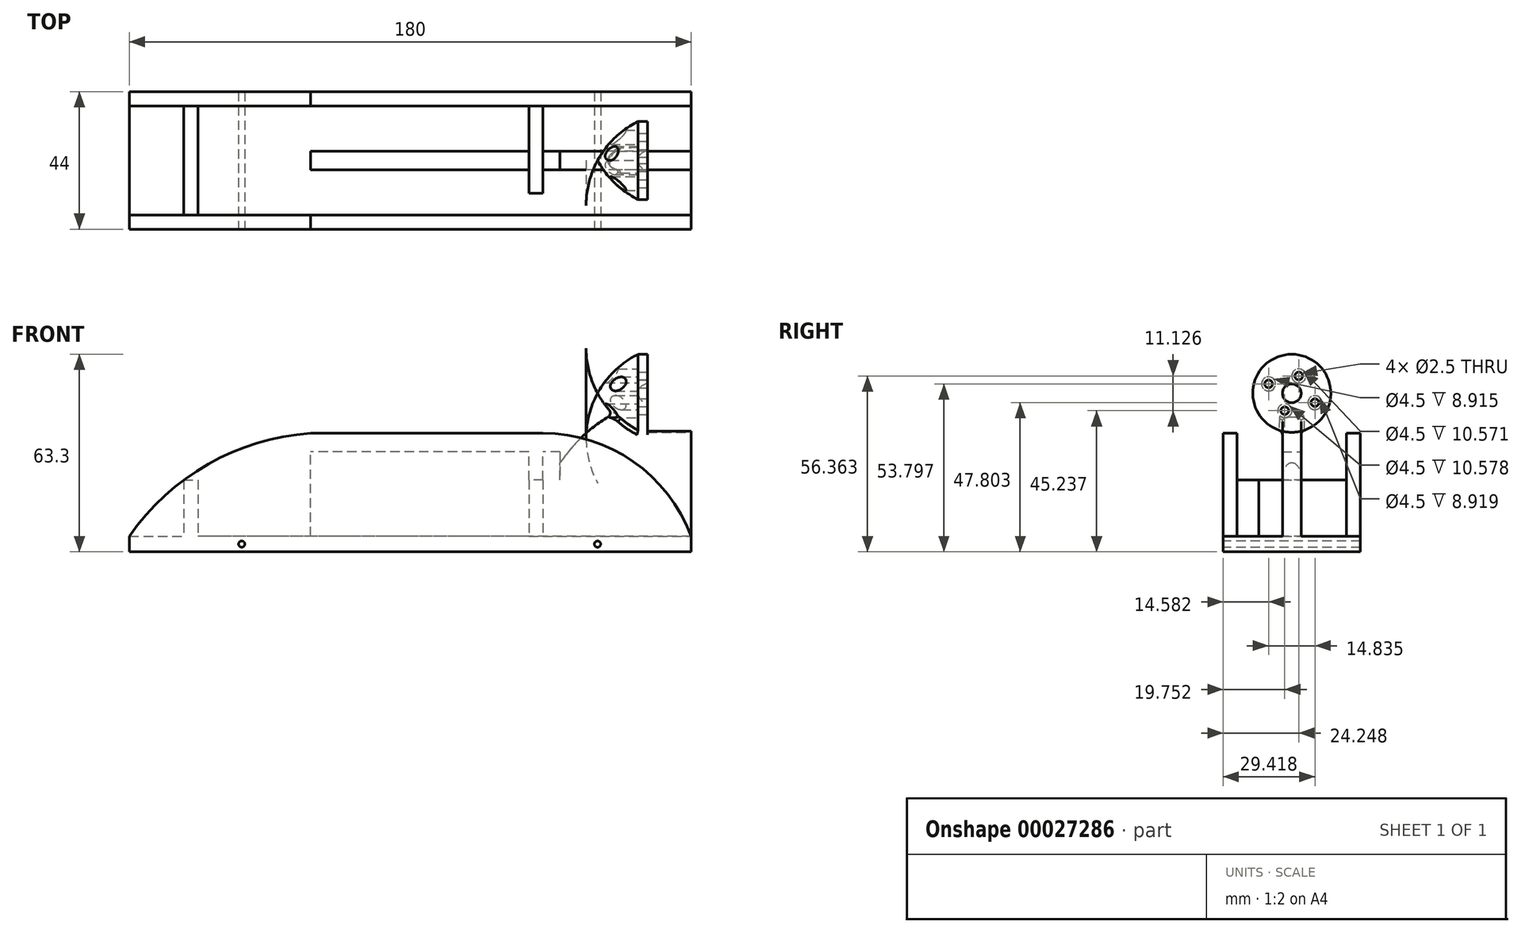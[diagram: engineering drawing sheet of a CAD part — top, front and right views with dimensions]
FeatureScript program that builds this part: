
annotation { "Feature Type Name" : "Feature", "Feature Type Description" : "" }
export const myFeature = defineFeature(function(context is Context, id is Id, definition is map)
    precondition{}
    {
        {
            var Q0;
            Q0=qCreatedBy(makeId("Top.planeOp"),FACE);
            var sketch = newSketch(context, id + "F0", { "sketchPlane" : qUnion([Q0])});
            skLineSegment(sketch, "E0.bottom", {"start": v(90, 22) * mm, "end": v(-90, 22) * mm});
            skLineSegment(sketch, "E0.top", {"start": v(90, -22) * mm, "end": v(-90, -22) * mm});
            skLineSegment(sketch, "E0.left", {"start": v(90, 22) * mm, "end": v(90, -22) * mm});
            skLineSegment(sketch, "E0.right", {"start": v(-90, 22) * mm, "end": v(-90, -22) * mm});
            skPoint(sketch, "E0.middle", {"position": v(0, 0) * mm});
            skSolve(sketch);
        }
        {
            var Q0;
            Q0=qSketchRegion(id+"F0",true);
            extrude(context, id + "F1", {"entities" : qUnion([Q0]), "depth" : 37 * mm});
        }
        {
            var Q0;
            Q0=makeQuery(id+"F1.opExtrude","SWEPT_FACE",FACE,{"disambiguationData":[OSD([sQuery(id+"F0.wireOp",EDGE,"E0.left")])]});
            var sketch = newSketch(context, id + "F2", { "sketchPlane" : qUnion([Q0])});
            skLineSegment(sketch, "E1", {"start": v(0, 0) * mm, "end": v(0, 50.8) * mm});
            skCircle(sketch, "E2", {"center": v(0, 50.8) * mm, "radius": 11.5 * mm});
            skCircle(sketch, "E3", {"center": v(0, 50.8) * mm, "radius": 50.8 * mm, "construction": true});
            skSolve(sketch);
        }
        {
            var Q0;
            Q0=qCreatedBy(makeId("Front.planeOp"),FACE);
            var sketch = newSketch(context, id + "F3", { "sketchPlane" : qUnion([Q0])});
            skLineSegment(sketch, "E4.0", {"start": v(90, 0) * mm, "end": v(90, 50.8) * mm});
            skLineSegment(sketch, "E5.0", {"start": v(-90, 37) * mm, "end": v(-90, 0) * mm});
            skLineSegment(sketch, "E6.0", {"start": v(90, 37) * mm, "end": v(-90, 37) * mm});
            skLineSegment(sketch, "E7", {"start": v(0, 37) * mm, "end": v(0, 0) * mm, "construction": true});
            skLineSegment(sketch, "E8", {"start": v(-90, 5) * mm, "end": v(90, 5) * mm});
            skSolve(sketch);
        }
        {
            var Q0;
            Q0=qSketchRegion(id+"F3",true);
            extrude(context, id + "F4", {"entities" : qUnion([Q0]), "operationType" : NewBodyOperationType.REMOVE, "oppositeDirection" : true, "depth" : 25 * mm, "hasSecondDirection" : true, "secondDirectionOppositeDirection" : false, "secondDirectionDepth" : 25 * mm});
        }
        {
            var Q0;
            Q0=qCreatedBy(makeId("Front.planeOp"),FACE);
            var sketch = newSketch(context, id + "F5", { "sketchPlane" : qUnion([Q0])});
            skLineSegment(sketch, "E9.top", {"start": v(48, 32) * mm, "end": v(-32, 32) * mm});
            skLineSegment(sketch, "E9.right", {"start": v(-32, 2) * mm, "end": v(-32, 32) * mm});
            skLineSegment(sketch, "E10", {"start": v(48, 32) * mm, "end": v(48, 2) * mm});
            skLineSegment(sketch, "E11", {"start": v(48, 2) * mm, "end": v(-32, 2) * mm});
            skSolve(sketch);
        }
        {
            var Q0;
            Q0=qSketchRegion(id+"F5",true);
            extrude(context, id + "F6", {"entities" : qUnion([Q0]), "depth" : (35 / 2) * mm, "hasSecondDirection" : true, "secondDirectionOppositeDirection" : true, "secondDirectionDepth" : 17.5 * mm});
        }
        {
            var Q0;
            {var subQ1=sQuery(id+"F0.wireOp",EDGE,"E0.left");var subQ6=makeQuery(id+"F1.opExtrude","SWEPT_EDGE",EDGE,{"disambiguationData":[OSD([sQuery(id+"F0.wireOp",EDGE,"E0.top"),subQ1])]});Q0=makeQuery(id+"F2.imprint","IMPRINT",FACE,{"disambiguationData":[TD([[makeQuery(id+"F2.imprint","IMPRINT",EDGE,{"derivedFrom":subQ6}),1.0]])]});}
            var sketch = newSketch(context, id + "F7", { "sketchPlane" : qUnion([Q0])});
            skLineSegment(sketch, "E12.bottom", {"start": v(-3, 50.8) * mm, "end": v(3, 50.8) * mm});
            skLineSegment(sketch, "E12.top", {"start": v(-3, 0) * mm, "end": v(3, 0) * mm});
            skLineSegment(sketch, "E12.left", {"start": v(-3, 50.8) * mm, "end": v(-3, 0) * mm});
            skLineSegment(sketch, "E12.right", {"start": v(3, 50.8) * mm, "end": v(3, 0) * mm});
            skPoint(sketch, "E12.middle", {"position": v(0, 25.4) * mm});
            skLineSegment(sketch, "E13.0", {"start": v(0, 0) * mm, "end": v(0, 50.8) * mm, "construction": true});
            skSolve(sketch);
        }
        {
            var Q0;
            Q0=qSketchRegion(id+"F7",true);
            var Q1;
            Q1=sQuery(id+"F7.wireOp",EDGE,"E12.top");
            revolve(context, id + "F8", {"operationType" : NewBodyOperationType.ADD, "entities" : qUnion([Q0]), "axis" : qUnion([Q1]), "revolveType" : RevolveType.ONE_DIRECTION, "oppositeDirection" : true, "angle" : 90 * degree});
        }
        {
            var Q0;
            Q0=makeQuery(id+"F2.imprint","IMPRINT",FACE,{"disambiguationData":[TD([[makeQuery(id+"F2.imprint","IMPRINT",EDGE,{"derivedFrom":sQuery(id+"F2.wireOp",EDGE,"E2")}),1.0]])]});
            var sketch = newSketch(context, id + "F9", { "sketchPlane" : qUnion([Q0])});
            skCircle(sketch, "E14.0", {"center": v(0, 50.8) * mm, "radius": 11.5 * mm, "construction": true});
            skCircle(sketch, "E15.0", {"center": v(0, 50.8) * mm, "radius": 12.5 * mm});
            skSolve(sketch);
        }
        {
            var Q0;
            Q0=qSketchRegion(id+"F9",true);
            extrude(context, id + "F10", {"entities" : qUnion([Q0]), "operationType" : NewBodyOperationType.REMOVE, "oppositeDirection" : true, "depth" : 14 * mm});
        }
        {
            var Q0;
            Q0=qCreatedBy(makeId("Front.planeOp"),FACE);
            var sketch = newSketch(context, id + "F11", { "sketchPlane" : qUnion([Q0])});
            skPoint(sketch, "E16.0", {"position": v(90, 50.8) * mm});
            skLineSegment(sketch, "E17", {"start": v(90, 50.8) * mm, "end": v(60, 50.8) * mm});
            skLineSegment(sketch, "E18", {"start": v(73, 50.8) * mm, "end": v(73, 38.3) * mm, "construction": true});
            skArc(sketch, "E19", {"start": v(60, 50.8) * mm, "mid": v(65.54, 43.55) * mm, "end": v(73, 38.3) * mm});
            skLineSegment(sketch, "E20.0", {"start": v(76, 38.3) * mm, "end": v(76, 50.8) * mm});
            skPoint(sketch, "E21.orphan", {"position": v(76, 48.83) * mm});
            skLineSegment(sketch, "E22", {"start": v(73, 38.3) * mm, "end": v(76, 38.3) * mm});
            skPoint(sketch, "E23.orphan", {"position": v(76, 38.67) * mm});
            skSolve(sketch);
        }
        {
            var Q0;
            Q0=qSketchRegion(id+"F11",true);
            var Q1;
            Q1=sQuery(id+"F11.wireOp",EDGE,"E17");
            revolve(context, id + "F12", {"operationType" : NewBodyOperationType.ADD, "entities" : qUnion([Q0]), "axis" : qUnion([Q1]), "revolveType" : RevolveType.FULL});
        }
        {
            var Q0;
            Q0=makeQuery(id+"F12.boolean.opBoolean","MERGE",FACE,{"derivedFrom":[makeQuery(id+"F10.boolean.opBoolean","COPY",FACE,{"derivedFrom":makeQuery(id+"F10.opExtrude","CAP_FACE",FACE,{"disambiguationData":[OSD([sQuery(id+"F9.wireOp",EDGE,"E15.0")])],"isStart":false})}),makeQuery(id+"F12.opRevolve","SWEPT_FACE",FACE,{"disambiguationData":[OSD([sQuery(id+"F11.wireOp",EDGE,"E20.0")])]})]});
            var sketch = newSketch(context, id + "F13", { "sketchPlane" : qUnion([Q0])});
            skLineSegment(sketch, "E24", {"start": v(7.42, 47.8) * mm, "end": v(-7.42, 53.8) * mm, "construction": true});
            skLineSegment(sketch, "E25", {"start": v(2.25, 56.36) * mm, "end": v(-2.25, 45.24) * mm, "construction": true});
            skCircle(sketch, "E26", {"center": v(-7.42, 53.8) * mm, "radius": 1.25 * mm});
            skCircle(sketch, "E27", {"center": v(2.25, 56.36) * mm, "radius": 1.25 * mm});
            skCircle(sketch, "E28", {"center": v(-2.25, 45.24) * mm, "radius": 1.25 * mm});
            skCircle(sketch, "E29", {"center": v(7.42, 47.8) * mm, "radius": 1.25 * mm});
            skSolve(sketch);
        }
        {
            var Q0;
            Q0=qSketchRegion(id+"F13",true);
            extrude(context, id + "F14", {"entities" : qUnion([Q0]), "operationType" : NewBodyOperationType.REMOVE, "endBound" : BoundingType.THROUGH_ALL, "oppositeDirection" : true, "depth" : 25 * mm});
        }
        {
            var Q0;
            Q0=makeQuery(id+"F12.boolean.opBoolean","MERGE",FACE,{"derivedFrom":[makeQuery(id+"F10.boolean.opBoolean","COPY",FACE,{"derivedFrom":makeQuery(id+"F10.opExtrude","CAP_FACE",FACE,{"disambiguationData":[OSD([sQuery(id+"F9.wireOp",EDGE,"E15.0")])],"isStart":false})}),makeQuery(id+"F12.opRevolve","SWEPT_FACE",FACE,{"disambiguationData":[OSD([sQuery(id+"F11.wireOp",EDGE,"E20.0")])]})]});
            var sketch = newSketch(context, id + "F15", { "sketchPlane" : qUnion([Q0])});
            skCircle(sketch, "E30", {"center": v(0, 50.8) * mm, "radius": 3 * mm});
            skSolve(sketch);
        }
        {
            var Q0;
            Q0=qSketchRegion(id+"F15",true);
            extrude(context, id + "F16", {"entities" : qUnion([Q0]), "operationType" : NewBodyOperationType.REMOVE, "oppositeDirection" : true, "depth" : 3 * mm});
        }
        {
            var Q0;
            Q0=makeQuery(id+"F16.boolean.opBoolean","COPY",EDGE,{"derivedFrom":makeQuery(id+"F16.opExtrude","CAP_EDGE",EDGE,{"disambiguationData":[OSD([sQuery(id+"F15.wireOp",EDGE,"E30")])],"isStart":false})});
            fillet(context, id + "F17", {"entities" : qUnion([Q0]), "radius" : 3 * mm, "tangentPropagation" : true, "allowEdgeOverflow" : false});
        }
        {
            var Q0;
            Q0=makeQuery(id+"F12.boolean.opBoolean","MERGE",FACE,{"derivedFrom":[makeQuery(id+"F10.boolean.opBoolean","COPY",FACE,{"derivedFrom":makeQuery(id+"F10.opExtrude","CAP_FACE",FACE,{"disambiguationData":[OSD([sQuery(id+"F9.wireOp",EDGE,"E15.0")])],"isStart":false})}),makeQuery(id+"F12.opRevolve","SWEPT_FACE",FACE,{"disambiguationData":[OSD([sQuery(id+"F11.wireOp",EDGE,"E20.0")])]})]});
            var sketch = newSketch(context, id + "F18", { "sketchPlane" : qUnion([Q0])});
            skCircle(sketch, "E31", {"center": v(-7.42, 53.8) * mm, "radius": 2.25 * mm});
            skCircle(sketch, "E32", {"center": v(2.25, 56.36) * mm, "radius": 2.25 * mm});
            skCircle(sketch, "E33", {"center": v(7.42, 47.8) * mm, "radius": 2.25 * mm});
            skCircle(sketch, "E34", {"center": v(-2.25, 45.24) * mm, "radius": 2.25 * mm});
            skSolve(sketch);
        }
        {
            var Q0;
            Q0=qSketchRegion(id+"F18",true);
            extrude(context, id + "F19", {"entities" : qUnion([Q0]), "operationType" : NewBodyOperationType.REMOVE, "endBound" : BoundingType.THROUGH_ALL, "oppositeDirection" : true, "depth" : 6.3 * mm, "hasSecondDirection" : true, "secondDirectionOppositeDirection" : true, "secondDirectionDepth" : 3 * mm});
        }
        {
            var Q0;
            {var subQ1=sQuery(id+"F0.wireOp",EDGE,"E0.left");var subQ6=makeQuery(id+"F1.opExtrude","SWEPT_EDGE",EDGE,{"disambiguationData":[OSD([sQuery(id+"F0.wireOp",EDGE,"E0.bottom"),subQ1])]});Q0=makeQuery(id+"F2.imprint","IMPRINT",FACE,{"disambiguationData":[TD([[makeQuery(id+"F2.imprint","IMPRINT",EDGE,{"derivedFrom":subQ6}),-1.0]])]});}
            var sketch = newSketch(context, id + "F20", { "sketchPlane" : qUnion([Q0])});
            skLineSegment(sketch, "E35", {"start": v(-28, 5) * mm, "end": v(-3, 5) * mm});
            skLineSegment(sketch, "E36.0", {"start": v(-3, 38.67) * mm, "end": v(-3, 5) * mm});
            skLineSegment(sketch, "E36.1", {"start": v(3, 38.67) * mm, "end": v(3, 5) * mm});
            skLineSegment(sketch, "E37.trimOffspring", {"start": v(3, 5) * mm, "end": v(28, 5) * mm});
            skLineSegment(sketch, "E38", {"start": v(-28, 5) * mm, "end": v(-28, 38.67) * mm});
            skLineSegment(sketch, "E39", {"start": v(-28, 38.67) * mm, "end": v(-3, 38.67) * mm});
            skLineSegment(sketch, "E40", {"start": v(28, 5) * mm, "end": v(28, 38.67) * mm});
            skLineSegment(sketch, "E41", {"start": v(28, 38.67) * mm, "end": v(3, 38.67) * mm});
            skSolve(sketch);
        }
        {
            var Q0;
            Q0=qSketchRegion(id+"F20",true);
            extrude(context, id + "F21", {"entities" : qUnion([Q0]), "operationType" : NewBodyOperationType.REMOVE, "endBound" : BoundingType.THROUGH_ALL, "oppositeDirection" : true, "depth" : 25 * mm});
        }
        {
            var Q0;
            Q0=qCreatedBy(makeId("Front.planeOp"),FACE);
            var sketch = newSketch(context, id + "F22", { "sketchPlane" : qUnion([Q0])});
            skCircle(sketch, "E42", {"center": v(-54, 2.5) * mm, "radius": 1 * mm});
            skCircle(sketch, "E43", {"center": v(60, 2.5) * mm, "radius": 1 * mm});
            skSolve(sketch);
        }
        {
            var Q0;
            Q0=qSketchRegion(id+"F22",true);
            extrude(context, id + "F23", {"entities" : qUnion([Q0]), "operationType" : NewBodyOperationType.REMOVE, "oppositeDirection" : true, "depth" : 25 * mm, "hasSecondDirection" : true, "secondDirectionOppositeDirection" : false, "secondDirectionDepth" : 25 * mm});
        }
        {
            var Q0;
            Q0=makeQuery(id+"F8.opRevolve","SWEPT_EDGE",EDGE,{"disambiguationData":[OSD([sQuery(id+"F7.wireOp",EDGE,"E12.bottom"),sQuery(id+"F7.wireOp",EDGE,"E12.left")])]});
            var Q1;
            Q1=makeQuery(id+"F8.opRevolve","SWEPT_EDGE",EDGE,{"disambiguationData":[OSD([sQuery(id+"F7.wireOp",EDGE,"E12.bottom"),sQuery(id+"F7.wireOp",EDGE,"E12.right")])]});
            fillet(context, id + "F24", {"entities" : qUnion([Q0, Q1]), "radius" : 2.9 * mm, "tangentPropagation" : true, "allowEdgeOverflow" : false});
        }
        {
            var Q0;
            Q0=makeQuery(id+"F24.opFillet","BLEND_EDGE",EDGE,{"blendedFrom":[makeQuery(id+"F8.opRevolve","SWEPT_EDGE",EDGE,{"disambiguationData":[OSD([sQuery(id+"F7.wireOp",EDGE,"E12.bottom"),sQuery(id+"F7.wireOp",EDGE,"E12.right")])]}),makeQuery(id+"F12.opRevolve","SWEPT_FACE",FACE,{"disambiguationData":[OSD([sQuery(id+"F11.wireOp",EDGE,"E19")])]})],"blendedInto":[makeQuery(id+"F12.opRevolve","SWEPT_FACE",FACE,{"disambiguationData":[OSD([sQuery(id+"F11.wireOp",EDGE,"E19")])]})]});
            var Q1;
            Q1=makeQuery(id+"F24.opFillet","BLEND_EDGE",EDGE,{"disambiguationData":[OD(1.0)],"blendedFrom":[makeQuery(id+"F8.opRevolve","SWEPT_EDGE",EDGE,{"disambiguationData":[OSD([sQuery(id+"F7.wireOp",EDGE,"E12.bottom"),sQuery(id+"F7.wireOp",EDGE,"E12.left")])]}),makeQuery(id+"F12.opRevolve","SWEPT_FACE",FACE,{"disambiguationData":[OSD([sQuery(id+"F11.wireOp",EDGE,"E19")])]})],"blendedInto":[makeQuery(id+"F12.opRevolve","SWEPT_FACE",FACE,{"disambiguationData":[OSD([sQuery(id+"F11.wireOp",EDGE,"E19")])]})]});
            var Q2;
            Q2=makeQuery(id+"F12.boolean.opBoolean","INTERSECT",EDGE,{"derivedFrom":[makeQuery(id+"F8.opRevolve","SWEPT_FACE",FACE,{"disambiguationData":[OSD([sQuery(id+"F7.wireOp",EDGE,"E12.right")])]}),makeQuery(id+"F12.opRevolve","SWEPT_FACE",FACE,{"disambiguationData":[OSD([sQuery(id+"F11.wireOp",EDGE,"E19")])]})]});
            var Q3;
            Q3=makeQuery(id+"F12.boolean.opBoolean","INTERSECT",EDGE,{"derivedFrom":[makeQuery(id+"F8.opRevolve","SWEPT_FACE",FACE,{"disambiguationData":[OSD([sQuery(id+"F7.wireOp",EDGE,"E12.right")])]}),makeQuery(id+"F12.opRevolve","SWEPT_FACE",FACE,{"disambiguationData":[OSD([sQuery(id+"F11.wireOp",EDGE,"E22")])]})]});
            var Q4;
            Q4=makeQuery(id+"F12.boolean.opBoolean","INTERSECT",EDGE,{"derivedFrom":[makeQuery(id+"F8.opRevolve","SWEPT_FACE",FACE,{"disambiguationData":[OSD([sQuery(id+"F7.wireOp",EDGE,"E12.left")])]}),makeQuery(id+"F12.opRevolve","SWEPT_FACE",FACE,{"disambiguationData":[OSD([sQuery(id+"F11.wireOp",EDGE,"E19")])]})]});
            var Q5;
            Q5=makeQuery(id+"F12.boolean.opBoolean","INTERSECT",EDGE,{"derivedFrom":[makeQuery(id+"F8.opRevolve","SWEPT_FACE",FACE,{"disambiguationData":[OSD([sQuery(id+"F7.wireOp",EDGE,"E12.left")])]}),makeQuery(id+"F12.opRevolve","SWEPT_FACE",FACE,{"disambiguationData":[OSD([sQuery(id+"F11.wireOp",EDGE,"E22")])]})]});
            fillet(context, id + "F25", {"entities" : qUnion([Q0, Q1, Q2, Q3, Q4, Q5]), "radius" : 1.5 * mm, "tangentPropagation" : true, "allowEdgeOverflow" : false});
        }
        {
            var Q0;
            Q0=makeQuery(id+"F4.boolean.opBoolean","COPY",FACE,{"derivedFrom":makeQuery(id+"F4.opExtrude","SWEPT_FACE",FACE,{"disambiguationData":[OSD([sQuery(id+"F3.wireOp",EDGE,"E8")])]})});
            var sketch = newSketch(context, id + "F26", { "sketchPlane" : qUnion([Q0])});
            skLineSegment(sketch, "E44.bottom", {"start": v(38, 17.5) * mm, "end": v(-68, 17.5) * mm});
            skLineSegment(sketch, "E44.top", {"start": v(38, -17.5) * mm, "end": v(-68, -17.5) * mm});
            skLineSegment(sketch, "E44.left", {"start": v(38, 17.5) * mm, "end": v(38, -10.5) * mm});
            skLineSegment(sketch, "E44.right", {"start": v(-68, 17.5) * mm, "end": v(-68, -17.5) * mm});
            skPoint(sketch, "E44.middle", {"position": v(-15, 0) * mm});
            skLineSegment(sketch, "E45.0", {"start": v(-90, 22) * mm, "end": v(90, 22) * mm});
            skLineSegment(sketch, "E46.0", {"start": v(-90, -22) * mm, "end": v(90, -22) * mm});
            skLineSegment(sketch, "E47", {"start": v(-72.6, 22) * mm, "end": v(-72.6, -22) * mm});
            skLineSegment(sketch, "E48", {"start": v(42.5, 22) * mm, "end": v(42.5, -10.5) * mm});
            skLineSegment(sketch, "E49", {"start": v(42.5, -17.5) * mm, "end": v(38, -17.5) * mm});
            skLineSegment(sketch, "E50", {"start": v(38, -10.5) * mm, "end": v(42.5, -10.5) * mm});
            skLineSegment(sketch, "E51.trimOffspring", {"start": v(42.5, -17.5) * mm, "end": v(42.5, -22) * mm});
            skSolve(sketch);
        }
        {
            var Q0;
            Q0 = qSketchRegion(id + "F26", true);
            extrude(context, id + "F27", {"entities" : qUnion([Q0]), "operationType" : NewBodyOperationType.ADD, "depth" : 18 * mm});
        }
        {
            var Q0;
            Q0=makeQuery(id+"F27.opExtrude","CAP_FACE",FACE,{"disambiguationData":[OSD([sQuery(id+"F26.wireOp",EDGE,"E44.bottom"),sQuery(id+"F26.wireOp",EDGE,"E44.top"),sQuery(id+"F26.wireOp",EDGE,"E44.left"),sQuery(id+"F26.wireOp",EDGE,"E44.right"),sQuery(id+"F26.wireOp",EDGE,"E45.0"),sQuery(id+"F26.wireOp",EDGE,"E46.0"),sQuery(id+"F26.wireOp",EDGE,"E47"),sQuery(id+"F26.wireOp",EDGE,"E48"),sQuery(id+"F26.wireOp",EDGE,"E49"),sQuery(id+"F26.wireOp",EDGE,"E50"),sQuery(id+"F26.wireOp",EDGE,"E51.trimOffspring")])],"isStart":false});
            var sketch = newSketch(context, id + "F28", { "sketchPlane" : qUnion([Q0])});
            skLineSegment(sketch, "E52.0.0", {"start": v(42.5, -10.5) * mm, "end": v(42.5, 22) * mm});
            skLineSegment(sketch, "E52.0.1", {"start": v(42.5, 22) * mm, "end": v(-32, 22) * mm});
            skLineSegment(sketch, "E52.0.3", {"start": v(-32, -22) * mm, "end": v(42.5, -22) * mm});
            skLineSegment(sketch, "E52.0.4", {"start": v(42.5, -22) * mm, "end": v(42.5, -17.5) * mm});
            skLineSegment(sketch, "E52.0.5", {"start": v(42.5, -17.5) * mm, "end": v(-32, -17.5) * mm});
            skLineSegment(sketch, "E52.0.7", {"start": v(-32, 17.5) * mm, "end": v(38, 17.5) * mm});
            skLineSegment(sketch, "E52.0.8", {"start": v(38, 17.5) * mm, "end": v(38, -10.5) * mm});
            skLineSegment(sketch, "E52.0.9", {"start": v(38, -10.5) * mm, "end": v(42.5, -10.5) * mm});
            skLineSegment(sketch, "E53", {"start": v(-32, 22) * mm, "end": v(-32, -22) * mm});
            skPoint(sketch, "E54.orphan", {"position": v(-68, 17.5) * mm});
            skPoint(sketch, "E55.orphan", {"position": v(-72.6, 22) * mm});
            skPoint(sketch, "E56.orphan", {"position": v(-72.6, -22) * mm});
            skPoint(sketch, "E57.orphan", {"position": v(-68, -17.5) * mm});
            skSolve(sketch);
        }
        {
            var Q0;
            Q0 = qSketchRegion(id + "F28", true);
            extrude(context, id + "F29", {"entities" : qUnion([Q0]), "operationType" : NewBodyOperationType.ADD, "depth" : 15 * mm});
        }
        {
            var Q0;
            Q0=makeQuery(id+"F29.boolean.opBoolean","MERGE",FACE,{"derivedFrom":[makeQuery(id+"F27.boolean.opBoolean","MERGE",FACE,{"derivedFrom":[makeQuery(id+"F1.opExtrude","SWEPT_FACE",FACE,{"disambiguationData":[OSD([sQuery(id+"F0.wireOp",EDGE,"E0.top")])]}),makeQuery(id+"F27.opExtrude","SWEPT_FACE",FACE,{"disambiguationData":[OSD([sQuery(id+"F26.wireOp",EDGE,"E46.0")])]})]}),makeQuery(id+"F29.opExtrude","SWEPT_FACE",FACE,{"disambiguationData":[OSD([sQuery(id+"F28.wireOp",EDGE,"E52.0.3")])]})]});
            var sketch = newSketch(context, id + "F30", { "sketchPlane" : qUnion([Q0])});
            skArc(sketch, "E58", {"start": v(-32, 38) * mm, "mid": v(-64.76, 28.11) * mm, "end": v(-90, 5) * mm});
            skArc(sketch, "E59", {"start": v(90, 5) * mm, "mid": v(71.42, 28.94) * mm, "end": v(42.5, 38) * mm});
            skLineSegment(sketch, "E60.0", {"start": v(-32, 38) * mm, "end": v(42.5, 38) * mm});
            skLineSegment(sketch, "E61", {"start": v(-90, 5) * mm, "end": v(90, 5) * mm});
            skSolve(sketch);
        }
        {
            var Q0;
            Q0 = qSketchRegion(id + "F30", true);
            var Q1;
            Q1=makeQuery(id+"F29.boolean.opBoolean","MERGE",FACE,{"derivedFrom":[makeQuery(id+"F27.opExtrude","SWEPT_FACE",FACE,{"disambiguationData":[OSD([sQuery(id+"F26.wireOp",EDGE,"E44.top"),sQuery(id+"F26.wireOp",EDGE,"E49")])]}),makeQuery(id+"F29.opExtrude","SWEPT_FACE",FACE,{"disambiguationData":[OSD([sQuery(id+"F28.wireOp",EDGE,"E52.0.5")])]})]});
            extrude(context, id + "F31", {"entities" : qUnion([Q0]), "operationType" : NewBodyOperationType.ADD, "endBound" : BoundingType.UP_TO_SURFACE, "oppositeDirection" : true, "endBoundEntityFace" : qUnion([Q1]), "depth" : 25 * mm});
        }
        {
            var Q0;
            Q0=makeQuery(id+"F29.boolean.opBoolean","MERGE",FACE,{"derivedFrom":[makeQuery(id+"F27.boolean.opBoolean","MERGE",FACE,{"derivedFrom":[makeQuery(id+"F1.opExtrude","SWEPT_FACE",FACE,{"disambiguationData":[OSD([sQuery(id+"F0.wireOp",EDGE,"E0.bottom")])]}),makeQuery(id+"F27.opExtrude","SWEPT_FACE",FACE,{"disambiguationData":[OSD([sQuery(id+"F26.wireOp",EDGE,"E45.0")])]})]}),makeQuery(id+"F29.opExtrude","SWEPT_FACE",FACE,{"disambiguationData":[OSD([sQuery(id+"F28.wireOp",EDGE,"E52.0.1")])]})]});
            var sketch = newSketch(context, id + "F32", { "sketchPlane" : qUnion([Q0])});
            skArc(sketch, "E62", {"start": v(-42.5, 38) * mm, "mid": v(-71.42, 28.94) * mm, "end": v(-90, 5) * mm});
            skArc(sketch, "E63.0", {"start": v(72.6, 23) * mm, "mid": v(53.38, 33.41) * mm, "end": v(32, 38) * mm});
            skArc(sketch, "E64.0", {"start": v(90, 5) * mm, "mid": v(82.04, 14.71) * mm, "end": v(72.6, 23) * mm});
            skLineSegment(sketch, "E65.0", {"start": v(32, 38) * mm, "end": v(-42.5, 38) * mm});
            skLineSegment(sketch, "E66", {"start": v(-90, 5) * mm, "end": v(90, 5) * mm});
            skSolve(sketch);
        }
        {
            var Q0;
            Q0 = qSketchRegion(id + "F32", true);
            var Q1;
            Q1=makeQuery(id+"F29.boolean.opBoolean","MERGE",FACE,{"derivedFrom":[makeQuery(id+"F27.opExtrude","SWEPT_FACE",FACE,{"disambiguationData":[OSD([sQuery(id+"F26.wireOp",EDGE,"E44.bottom")])]}),makeQuery(id+"F29.opExtrude","SWEPT_FACE",FACE,{"disambiguationData":[OSD([sQuery(id+"F28.wireOp",EDGE,"E52.0.7")])]})]});
            extrude(context, id + "F33", {"entities" : qUnion([Q0]), "operationType" : NewBodyOperationType.ADD, "endBound" : BoundingType.UP_TO_SURFACE, "oppositeDirection" : true, "endBoundEntityFace" : qUnion([Q1]), "depth" : 25 * mm});
        }
        {
            var Q0;
            Q0=makeQuery(id+"F29.opExtrude","CAP_FACE",FACE,{"disambiguationData":[OSD([sQuery(id+"F28.wireOp",EDGE,"E52.0.0"),sQuery(id+"F28.wireOp",EDGE,"E52.0.1"),sQuery(id+"F28.wireOp",EDGE,"E52.0.7"),sQuery(id+"F28.wireOp",EDGE,"E52.0.8"),sQuery(id+"F28.wireOp",EDGE,"E52.0.9"),sQuery(id+"F28.wireOp",EDGE,"E53")])],"isStart":false});
            var sketch = newSketch(context, id + "F34", { "sketchPlane" : qUnion([Q0])});
            skLineSegment(sketch, "E67", {"start": v(38, 17.5) * mm, "end": v(42.5, 17.5) * mm});
            skLineSegment(sketch, "E68.0", {"start": v(38, 17.5) * mm, "end": v(38, -10.5) * mm});
            skLineSegment(sketch, "E69.0", {"start": v(38, -10.5) * mm, "end": v(42.5, -10.5) * mm});
            skPoint(sketch, "E70.0", {"position": v(42.5, -3) * mm});
            skLineSegment(sketch, "E71.0", {"start": v(42.5, 17.5) * mm, "end": v(42.5, -10.5) * mm});
            skSolve(sketch);
        }
        {
            var Q0;
            Q0 = qSketchRegion(id + "F34", true);
            var Q1;
            Q1=makeQuery(id+"F27.opExtrude","CAP_FACE",FACE,{"disambiguationData":[OSD([sQuery(id+"F26.wireOp",EDGE,"E44.bottom"),sQuery(id+"F26.wireOp",EDGE,"E44.top"),sQuery(id+"F26.wireOp",EDGE,"E44.left"),sQuery(id+"F26.wireOp",EDGE,"E44.right"),sQuery(id+"F26.wireOp",EDGE,"E45.0"),sQuery(id+"F26.wireOp",EDGE,"E46.0"),sQuery(id+"F26.wireOp",EDGE,"E47"),sQuery(id+"F26.wireOp",EDGE,"E48"),sQuery(id+"F26.wireOp",EDGE,"E49"),sQuery(id+"F26.wireOp",EDGE,"E50"),sQuery(id+"F26.wireOp",EDGE,"E51.trimOffspring")])],"isStart":false});
            extrude(context, id + "F35", {"entities" : qUnion([Q0]), "operationType" : NewBodyOperationType.REMOVE, "endBound" : BoundingType.UP_TO_SURFACE, "oppositeDirection" : true, "endBoundEntityFace" : qUnion([Q1]), "depth" : 25 * mm});
        }
    });
